# Revit family: Ultrablade Exit_Hosted_R18
name_source: partatom
category: Lighting Fixtures
revit_build: Autodesk Revit 2018 (Build: 20170223_1515(x64)
units: mm (PartAtom-declared; Revit-internal decimal feet)

## family parameters
Cut with Voids When Loaded = No
Host = Face
Light Source = Yes
Part Type = Normal
Room Calculation Point = No
Round Connector Dimension = Use Diameter
Shared = No

## types (15) — shared parameters
Annotation Direction = Exit_Annotation : Double Sided Exit Luminaire
Apparent Load = 5 W
Ballast = Electronic
Ceiling Depth = 95 mm
Color Filter = 16777215
Default Elevation = 1219 mm
Description = LED Premium Theatre Ultrablade Exit
Diffuser = All directional inserts included in the box
Dimming Lamp Color Temperature Shift = <None>
Double Sided = Yes
Emit Shape Visible in Rendering = No
Emit from Circle Diameter = 480 mm  [stored 1.5748 ft]
Finish = White plastic cover plate
Length = 480 mm  [stored 1.5748 ft]
Manufacturer = Clevertronics
Model = ZUBLED-TH-DS
Mounting = Recessed Ceiling Single-Sided & Double-Sided
Operating Mode = Maintained
Operating Voltage = 240 V
Photometric Web File = Premium LED Ultrablade Exit.ies
Sign Direction = Sign : Exit
Single Sided = No
Tilt Angle = -90.00°
Viewing Distance = 24000 mm  [stored 78.7402 ft]
Wattage Comments = Standby
Width = 110 mm  [stored 0.360892 ft]

## per-type parameters (varying)
| type | AS2293 | Battery | Charging Method | Inverter Board | Lamp | Power Consumption | Testing System | Zoneworks Node |
| ZUBLED | C0=D5 C90=E3.2 | P/N: 1510160, 6 x Sub C, High Temp NiCd | Dual Rate | P/N: 8002015, PCA Zoneworks plug-in compatible | P/N: 8002170, 24 x high intensity, low energy LED, surface mounted onto a replaceable lamp bar - 50,000hour
lamp bar - 50,000hour | 5 W | Zoneworks Computerised Testing System | P/N: 8001450, Zoneworks Powerline Node |
| CUBLED-ZW | C0=D5 C90=EB10 | P/N: 1550052, LP  3.2V 3.2 Ahr | Intelligent current limited constant voltage | P/N: 8002345, PCA Lithium UBlade Driver #CT10164-L4 | P/N: 8002175, 24 DLED UB LED Strip #CT10156-D2 | 4 W | Zoneworks Computerised Testing System | P/N: 8001450, Zoneworks Powerline Node |
| PUBLED | C0=D5 C90=E3.2 | P/N: 1510160, 6 x Sub C, High Temp NiCd | Dual Rate | P/N: 8002015, PCA Zoneworks plug-in compatible | P/N: 8002170, 24 x high intensity, low energy LED, surface mounted onto a replaceable lamp bar - 50,000hour
lamp bar - 50,000hour | 4 W | Manual Test Switch |  |
| ZUBLED-DALI | C0=D5 C90=E3.2 | P/N: 1510160, 6 x Sub C, High Temp NiCd | Dual Rate | P/N: 8002015, PCA Zoneworks plug-in compatible | P/N: 8002170, 24 x high intensity, low energy LED, surface mounted onto a replaceable lamp bar - 50,000hour
lamp bar - 50,000hour | 5 W | DALI Compatible Testing | P/N: 8002200, DALI Node |
| ZUBLED-DATA | C0=D5 C90=E3.2 | P/N: 1510160, 6 x Sub C, High Temp NiCd | Dual Rate | P/N: 8002015, PCA Zoneworks plug-in compatible | P/N: 8002170, 24 x high intensity, low energy LED, surface mounted onto a replaceable lamp bar - 50,000hour
lamp bar - 50,000hour | 5 W | Zoneworks DATA Testing | P/N: 8001455, Zoneworks DATA Node |
| DUBLED | C0=D5 C90=E3.2 | P/N: 1510160, 6 x Sub C, High Temp NiCd | Dual Rate | P/N: 8002015, PCA Zoneworks plug-in compatible | P/N: 8002170, 24 x high intensity, low energy LED, surface mounted onto a replaceable lamp bar - 50,000hour
lamp bar - 50,000hour | 5 W | Clevertest | P/N: 8001730, Clevertest Node |
| CUBLED-DATA | C0=D5 C90=B10 | P/N: 1550052, LP  3.2V 3.2 Ahr | Intelligent current limited constant voltage | P/N: 8002345, PCA Lithium UBlade Driver #CT10164-L4 | P/N: 8002175, 24 DLED UB LED Strip #CT10156-D2 | 4 W | Zoneworks DATA Testing | P/N: 8001455, Zoneworks Data Node |
| CUBLED-DALI | C0=D5 C90=B10 | P/N: 1550052, LP  3.2V 3.2 Ahr | Intelligent current limited constant voltage | P/N: 8002345, PCA Lithium UBlade Driver #CT10164-L4 | P/N: 8002175, 24 DLED UB LED Strip #CT10156-D2 | 4 W | DALI Compatible Testing | P/N: 8002200, DALI Node |
| CUBLED-CT | C0=D5 C90=B10 | P/N: 1550052, LP  3.2V 3.2 Ahr | Intelligent current limited constant voltage | P/N: 8002345, PCA Lithium UBlade Driver #CT10164-L4 | P/N: 8002175, 24 DLED UB LED Strip #CT10156-D2 | 4 W | Clevertest | P/N: 8001730, Clevertest Node |
| CUBLED | C0=D5 C90=B10 | P/N: 1550052, LP  3.2V 3.2 Ahr | Intelligent current limited constant voltage | P/N: 8002345, PCA Lithium UBlade Driver #CT10164-L4 | P/N: 8002175, 24 DLED UB LED Strip #CT10156-D2 | 4 W | Manual Test Switch |  |
| LUBLED | C0=D5 C90=B10 | P/N: 1530050, L10 3.3V 2.5 Ahr | Intelligent current limited constant voltage | P/N: 8002345, PCA Lithium UBlade Driver #CT10164-L4 | P/N: 8002175, 24 DLED UB LED Strip #CT10156-D2 | 4 W | Manual Test Switch |  |
| LUBLED-CT | C0=D5 C90=B10 | P/N: 1530052, L10  3.3V 2.5 Ahr | Intelligent current limited constant voltage | P/N: 8002345, PCA Lithium UBlade Driver #CT10164-L4 | P/N: 8002175, 24 DLED UB LED Strip #CT10156-D2 | 4 W | Clevertest | P/N: 8001730, Clevertest Node |
| LUBLED-DALI | C0=D5 C90=B10 | P/N: 1530052, L10  3.3V 2.5 Ahr | Intelligent current limited constant voltage | P/N: 8002345, PCA Lithium UBlade Driver #CT10164-L4 | P/N: 8002175, 24 DLED UB LED Strip #CT10156-D2 | 4 W | DALI Compatible Testing | P/N: 8002200, DALI Node |
| LUBLED-DATA | C0=D5 C90=B10 | P/N: 1530052, L10  3.3V 2.5 Ahr | Intelligent current limited constant voltage | P/N: 8002345, PCA Lithium UBlade Driver #CT10164-L4 | P/N: 8002175, 24 DLED UB LED Strip #CT10156-D2 | 4 W | Zoneworks DATA Testing | P/N: 8001455, Zoneworks Data Node |
| LUBLED-ZW | C0=D5 C90=B10 | P/N: 1530052, L10  3.3V 2.5 Ahr | Intelligent current limited constant voltage | P/N: 8002345, PCA Lithium UBlade Driver #CT10164-L4 | P/N: 8002175, 24 DLED UB LED Strip #CT10156-D2 | 4 W | Zoneworks Computerised Testing | P/N: 8001450, Zoneworks Powerline Node |

note: [stored X ft] marks values corroborated as IEEE doubles in the binary element streams (Revit-internal decimal feet)

## geometry (parser evidence)
native form markers: Sweep x4
no freeform markers — native parametric forms only
